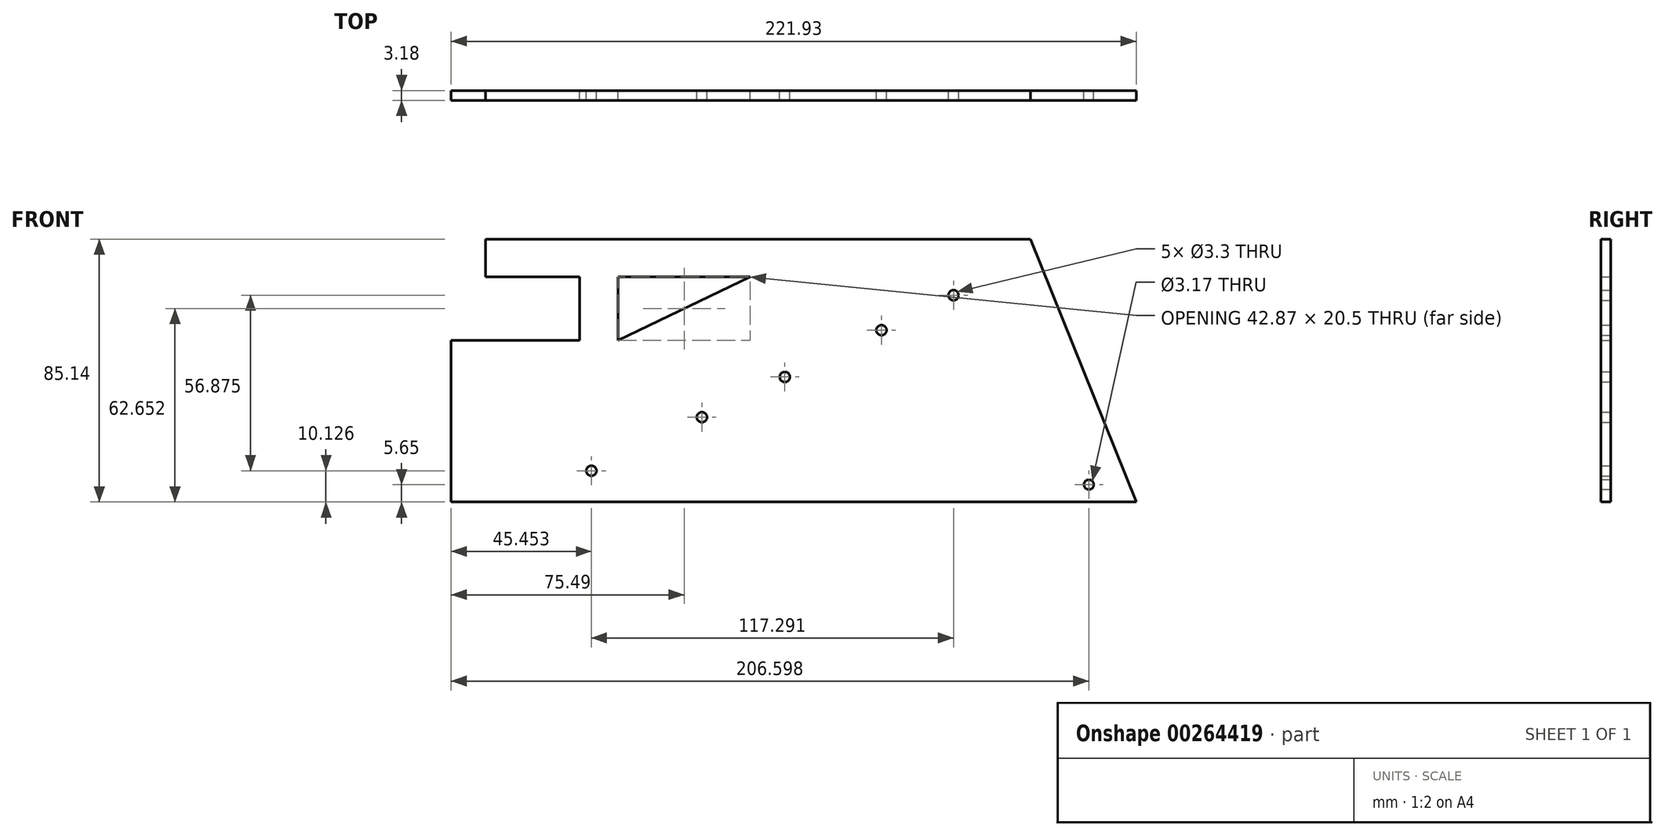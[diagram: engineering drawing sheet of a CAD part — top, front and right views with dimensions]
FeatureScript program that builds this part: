
annotation { "Feature Type Name" : "Feature", "Feature Type Description" : "" }
export const myFeature = defineFeature(function(context is Context, id is Id, definition is map)
    precondition{}
    {
        {
            var Q0;
            Q0=qCreatedBy(makeId("Front.planeOp"),FACE);
            var sketch = newSketch(context, id + "F0", { "sketchPlane" : qUnion([Q0])});
            skLineSegment(sketch, "E0.bottom", {"start": v(-9.46, 66.7) * mm, "end": v(75.07, 66.7) * mm});
            skCircle(sketch, "E1", {"center": v(-67.16, -8.31) * mm, "radius": 1.65 * mm});
            skCircle(sketch, "E2", {"center": v(-31.37, 9.04) * mm, "radius": 1.65 * mm});
            skCircle(sketch, "E3", {"center": v(-4.49, 22.07) * mm, "radius": 1.65 * mm});
            skCircle(sketch, "E4", {"center": v(26.8, 37.25) * mm, "radius": 1.65 * mm});
            skCircle(sketch, "E5", {"center": v(50.13, 48.56) * mm, "radius": 1.65 * mm});
            skPoint(sketch, "E6.orphan", {"position": v(127.58, -69.58) * mm});
            skLineSegment(sketch, "E7", {"start": v(109.32, -18.44) * mm, "end": v(-112.6, -18.44) * mm});
            skLineSegment(sketch, "E8", {"start": v(75.07, 66.7) * mm, "end": v(109.32, -18.44) * mm});
            skLineSegment(sketch, "E9", {"start": v(-112.6, 33.96) * mm, "end": v(-112.6, -18.44) * mm});
            skLineSegment(sketch, "E10", {"start": v(-112.6, 33.96) * mm, "end": v(-71, 33.96) * mm});
            skLineSegment(sketch, "E11", {"start": v(-71, 33.96) * mm, "end": v(-71, 54.46) * mm});
            skLineSegment(sketch, "E12", {"start": v(-71, 54.46) * mm, "end": v(-101.43, 54.46) * mm});
            skLineSegment(sketch, "E13", {"start": v(-101.43, 54.46) * mm, "end": v(-101.43, 66.7) * mm});
            skLineSegment(sketch, "E14", {"start": v(-101.43, 66.7) * mm, "end": v(-9.46, 66.7) * mm});
            skLineSegment(sketch, "E15", {"start": v(-58.56, 54.46) * mm, "end": v(-58.56, 33.96) * mm});
            skLineSegment(sketch, "E16", {"start": v(-58.56, 33.96) * mm, "end": v(-15.68, 54.46) * mm});
            skLineSegment(sketch, "E17", {"start": v(-15.68, 54.46) * mm, "end": v(-58.56, 54.46) * mm});
            skCircle(sketch, "E18", {"center": v(93.99, -12.79) * mm, "radius": 1.59 * mm});
            skSolve(sketch);
        }
        {
            var Q0;
            Q0 = qSketchRegion(id + "F0", true);
            extrude(context, id + "F1", {"entities" : qUnion([Q0]), "depth" : 3.17 * mm});
        }
    });
